# Revit family: НЕВАТОМ_Neiva 2 подвесная C-Е-R 1000, Версия 2
name_source: partatom
category: Оборудование
revit_build: Autodesk Revit 2017 (Build: 20170118_1100(x64)
units: mm (PartAtom-declared; Revit-internal decimal feet)

## family parameters
Всегда вертикально = Нет
На основе рабочей плоскости = Да
Общий = Нет
При загрузке вырезать с полостями = Нет
Размер круглого соединителя = Использовать диаметр
Тип детали = Нормальный
Точка расчета площади = Нет

## types (1)
- C-1000-E-R
    ADSK_Классификация нагрузок = Двигатель
    ADSK_Количество = 1
    ADSK_Количество фаз = 1
    ADSK_Коэффициент мощности = 0.8
    ADSK_Масса = 62
    ADSK_Наименование = C-1500-E-R
    ADSK_Напряжение = 230 В
    ADSK_Номинальная мощность = 230 Вт
    ADSK_Полная мощность = 288 В·А
    ADSK_Потеря давления воздуха = 0.0 Па
    ADSK_Размер_Высота = 412 мм
    ADSK_Размер_Длина = 1100 мм
    ADSK_Размер_Ширина = 670 мм
    ADSK_Расход воздуха = 0.0 м³/ч
    ADSK_Ток = 5 А
    B = 670 мм
    D кабельного ввода PG 21 = 32 мм
    D кабельного ввода PG 36 = 50 мм
    H = 412 мм
    H щита = 412 мм
    L = 1100 мм
    Nevatom_Мощность нагревателя = 24000 Вт
    Nevatom_Напорная характеристика, P = 0.0 Па
    Nevatom_Напорная характеристика, Р1 = 1000.0 Па
    Nevatom_Производительность = 1000-1800 м³/ч
    b длина = 835 мм
    c = 131 мм
    А1 = 630 мм
    А6 = 320 мм
    Отметка по умолчанию = 0 мм
    а ширина = 100 мм
    длина между креплением = 1062 мм
